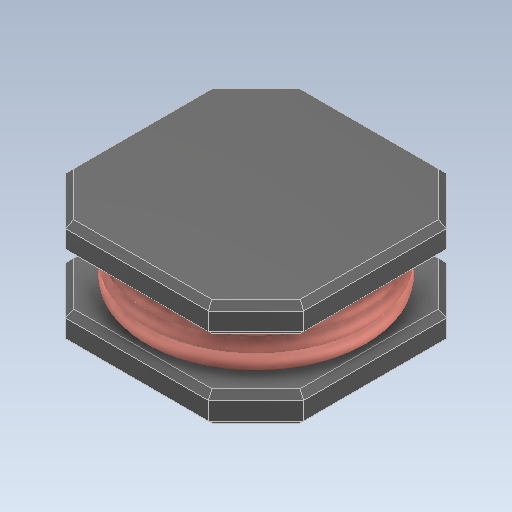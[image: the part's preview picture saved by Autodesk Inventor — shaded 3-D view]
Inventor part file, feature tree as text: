
AUTODESK INVENTOR PART (.ipt)
format: ipt  version: 2021 (Build 250183000, 183)  size: 252,416 bytes
history: native  units: mm
features: helix x3, other x1
ambient origin geometry x8: Origin, YZ Plane, XZ Plane, XY Plane, X Axis, Y Axis, Z Axis, Center Point
bodies: Solid1 (feature_tree), Solid2 (feature_tree), Solid3 (feature_tree), Solid4 (feature_tree)
feature tree (4):
  other  "BASES C"
  helix  "Coil"  [1 undecoded]
  helix  "COIL P[1]"  [1 undecoded]
  helix  "COIL P[2]"  [1 undecoded]
note: 3 required parameter values undecoded (feature->parameter linkage not recoverable at this tier; creation-order binding heuristic only, values carry confidence <= 0.55)
